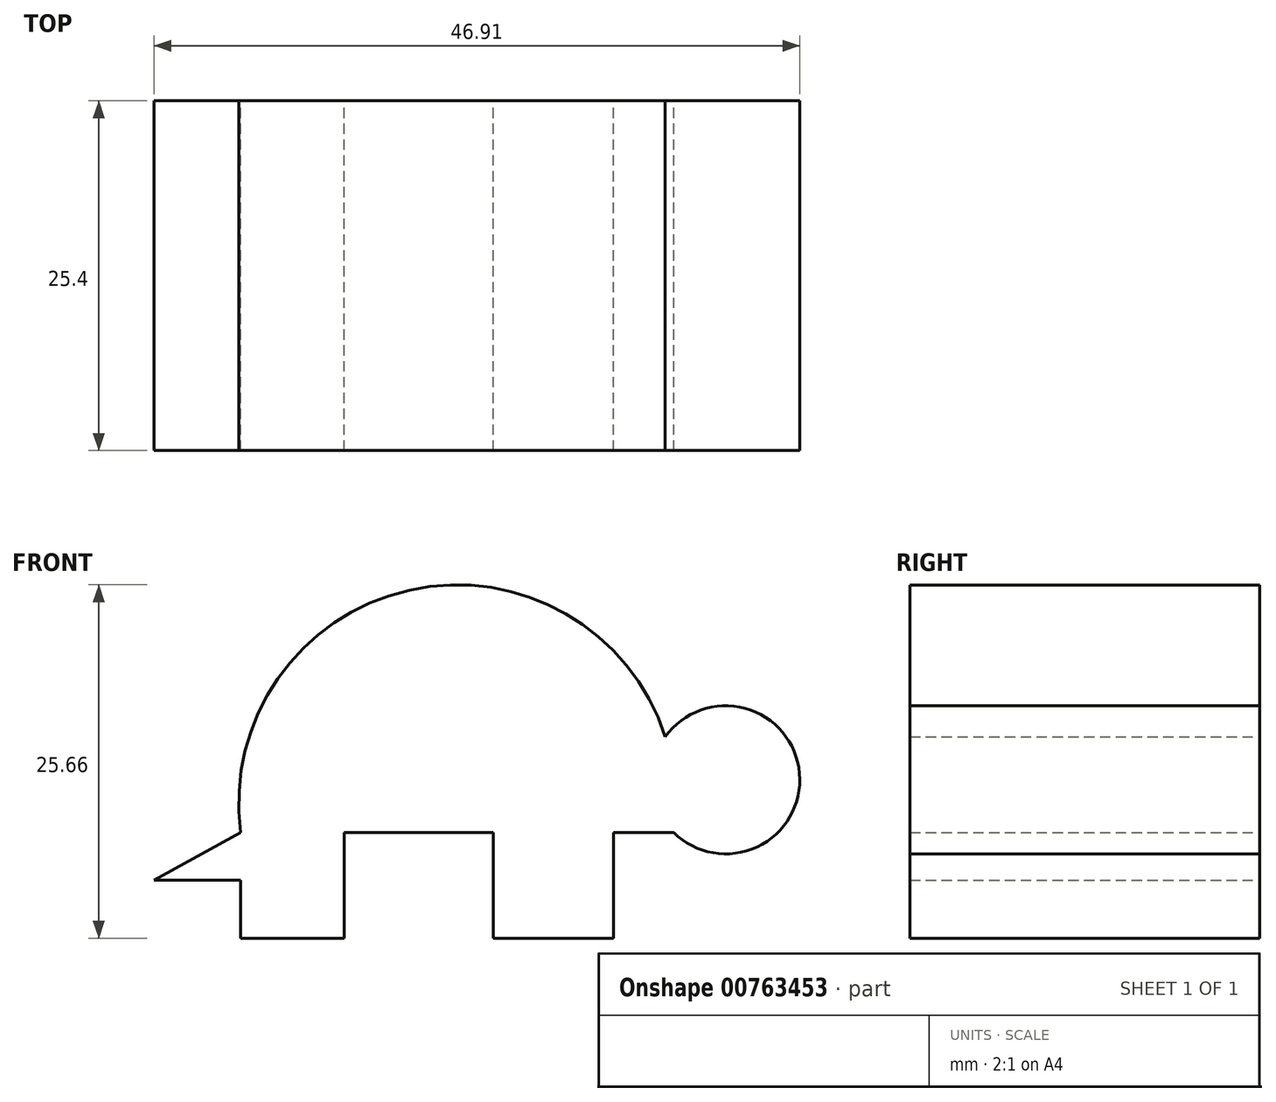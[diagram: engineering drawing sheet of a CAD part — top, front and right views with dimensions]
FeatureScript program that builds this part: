
annotation { "Feature Type Name" : "Feature", "Feature Type Description" : "" }
export const myFeature = defineFeature(function(context is Context, id is Id, definition is map)
    precondition{}
    {
        {
            var Q0;
            Q0=qCreatedBy(makeId("Front.planeOp"),FACE);
            var sketch = newSketch(context, id + "F0", { "sketchPlane" : qUnion([Q0])});
            skArc(sketch, "E0", {"start": v(0, 0) * mm, "mid": v(-15.72, 17.99) * mm, "end": v(-31.43, 0) * mm});
            skLineSegment(sketch, "E1", {"start": v(-31.43, 0) * mm, "end": v(0, 0) * mm});
            skArc(sketch, "E2", {"start": v(0, 0) * mm, "mid": v(9.14, 4.3) * mm, "end": v(-0.6, 6.95) * mm});
            skLineSegment(sketch, "E3", {"start": v(-31.43, 0) * mm, "end": v(-37.75, -3.46) * mm});
            skLineSegment(sketch, "E4", {"start": v(-37.75, -3.46) * mm, "end": v(-31.43, -3.46) * mm});
            skLineSegment(sketch, "E5", {"start": v(-31.43, -3.46) * mm, "end": v(-31.43, 0) * mm});
            skLineSegment(sketch, "E6", {"start": v(-31.43, -7.67) * mm, "end": v(-23.91, -7.67) * mm});
            skLineSegment(sketch, "E7", {"start": v(-23.91, -7.67) * mm, "end": v(-23.91, 0) * mm});
            skLineSegment(sketch, "E8", {"start": v(-23.91, 0) * mm, "end": v(-13.08, 0) * mm});
            skLineSegment(sketch, "E9", {"start": v(-13.08, 0) * mm, "end": v(-13.08, -7.67) * mm});
            skLineSegment(sketch, "E10", {"start": v(-13.08, -7.67) * mm, "end": v(-4.36, -7.67) * mm});
            skLineSegment(sketch, "E11", {"start": v(-4.36, -7.67) * mm, "end": v(-4.36, 0) * mm});
            skLineSegment(sketch, "E12", {"start": v(-31.43, -7.67) * mm, "end": v(-31.43, 0) * mm});
            skSolve(sketch);
        }
        {
            var Q0;
            Q0 = qSketchRegion(id + "F0", true);
            extrude(context, id + "F1", {"entities" : qUnion([Q0]), "depth" : 25.4 * mm, "offsetDistance" : 25.4 * mm});
        }
    });
